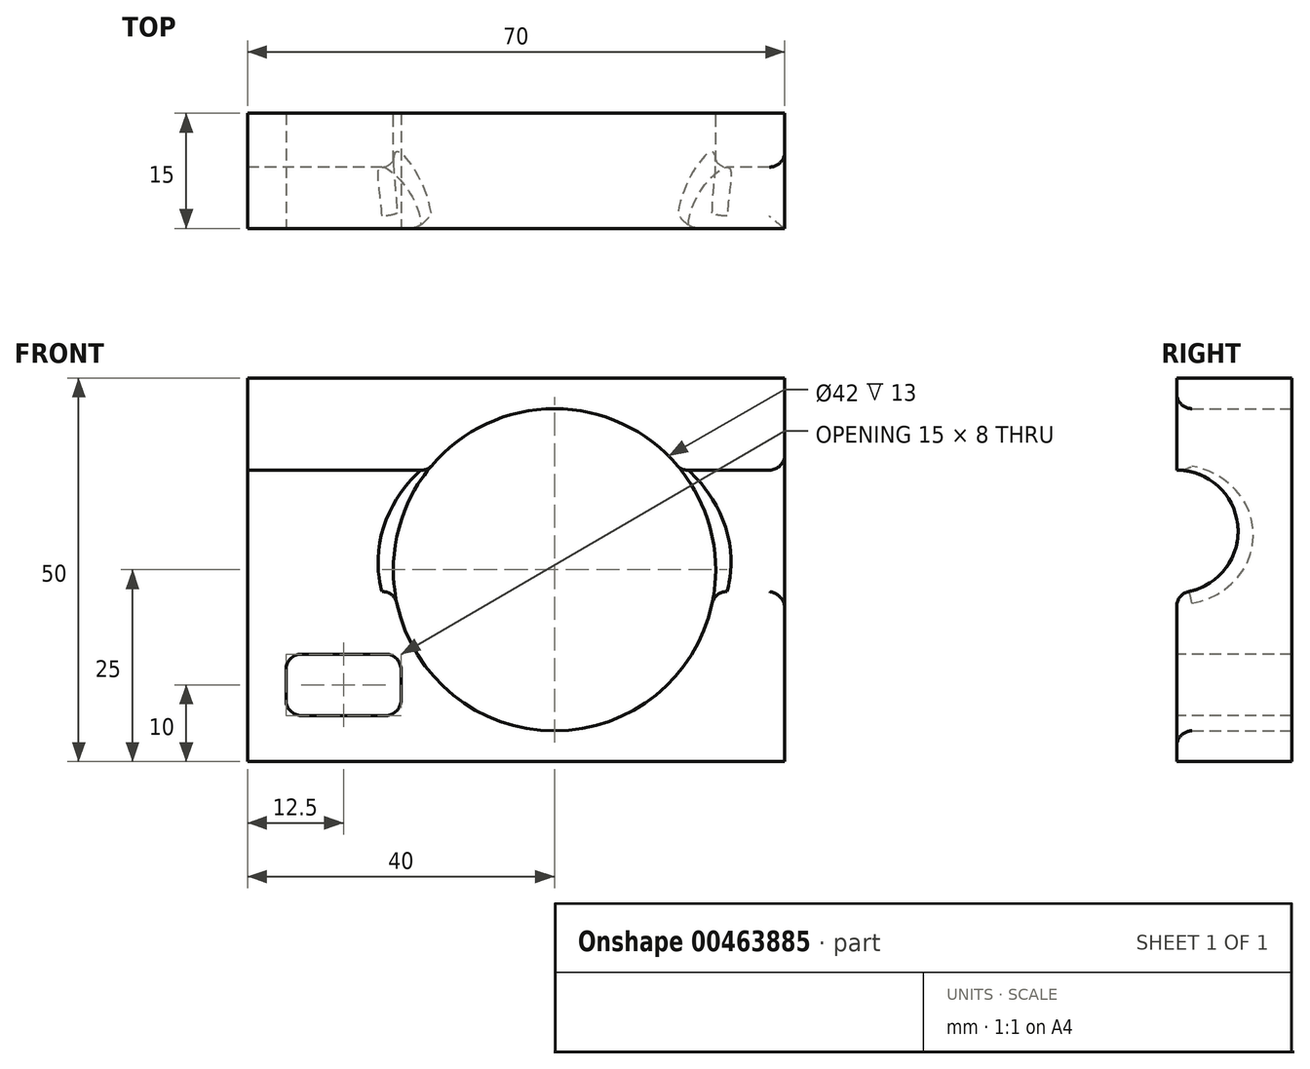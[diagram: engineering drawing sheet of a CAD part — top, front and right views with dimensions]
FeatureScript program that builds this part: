
annotation { "Feature Type Name" : "Feature", "Feature Type Description" : "" }
export const myFeature = defineFeature(function(context is Context, id is Id, definition is map)
    precondition{}
    {
        {
            var Q0;
            Q0=qCreatedBy(makeId("Front.planeOp"),FACE);
            var sketch = newSketch(context, id + "F0", { "sketchPlane" : qUnion([Q0])});
            skCircle(sketch, "E0", {"center": v(0, 0) * mm, "radius": 21 * mm});
            skLineSegment(sketch, "E1.bottom", {"start": v(-40, 25) * mm, "end": v(30, 25) * mm});
            skLineSegment(sketch, "E1.top", {"start": v(-40, -25) * mm, "end": v(30, -25) * mm});
            skLineSegment(sketch, "E1.left", {"start": v(-40, 25) * mm, "end": v(-40, -25) * mm});
            skLineSegment(sketch, "E1.right", {"start": v(30, 25) * mm, "end": v(30, -25) * mm});
            skSolve(sketch);
        }
        {
            var Q0;
            Q0 = qSketchRegion(id + "F0", true);
            extrude(context, id + "F1", {"entities" : qUnion([Q0]), "depth" : 15 * mm});
        }
        {
            var Q0;
            Q0=makeQuery(id+"F1.opExtrude","CAP_FACE",FACE,{"disambiguationData":[OSD([sQuery(id+"F0.wireOp",EDGE,"E0"),sQuery(id+"F0.wireOp",EDGE,"E1.bottom"),sQuery(id+"F0.wireOp",EDGE,"E1.top"),sQuery(id+"F0.wireOp",EDGE,"E1.left"),sQuery(id+"F0.wireOp",EDGE,"E1.right")])],"isStart":false});
            var sketch = newSketch(context, id + "F2", { "sketchPlane" : qUnion([Q0])});
            skLineSegment(sketch, "E2.bottom", {"start": v(-33, -11) * mm, "end": v(-22, -11) * mm});
            skLineSegment(sketch, "E2.top", {"start": v(-33, -19) * mm, "end": v(-22, -19) * mm});
            skLineSegment(sketch, "E2.left", {"start": v(-35, -13) * mm, "end": v(-35, -17) * mm});
            skLineSegment(sketch, "E2.right", {"start": v(-20, -13) * mm, "end": v(-20, -17) * mm});
            skPoint(sketch, "E3.visualSharp", {"position": v(-35, -11) * mm});
            skArc(sketch, "E3.filletArc", {"start": v(-33, -11) * mm, "mid": v(-34.41, -11.59) * mm, "end": v(-35, -13) * mm});
            skPoint(sketch, "E4.visualSharp", {"position": v(-20, -11) * mm});
            skArc(sketch, "E4.filletArc", {"start": v(-20, -13) * mm, "mid": v(-20.59, -11.59) * mm, "end": v(-22, -11) * mm});
            skPoint(sketch, "E5.visualSharp", {"position": v(-35, -19) * mm});
            skArc(sketch, "E5.filletArc", {"start": v(-35, -17) * mm, "mid": v(-34.41, -18.41) * mm, "end": v(-33, -19) * mm});
            skPoint(sketch, "E6.visualSharp", {"position": v(-20, -19) * mm});
            skArc(sketch, "E6.filletArc", {"start": v(-22, -19) * mm, "mid": v(-20.59, -18.41) * mm, "end": v(-20, -17) * mm});
            skSolve(sketch);
        }
        {
            var Q0;
            Q0 = qSketchRegion(id + "F2", true);
            extrude(context, id + "F3", {"entities" : qUnion([Q0]), "operationType" : NewBodyOperationType.REMOVE, "endBound" : BoundingType.THROUGH_ALL, "oppositeDirection" : true, "depth" : 25 * mm, "offsetDistance" : 25 * mm});
        }
        {
            var Q0;
            Q0=makeQuery(id+"F1.opExtrude","SWEPT_FACE",FACE,{"disambiguationData":[OSD([sQuery(id+"F0.wireOp",EDGE,"E1.left")])]});
            var sketch = newSketch(context, id + "F4", { "sketchPlane" : qUnion([Q0])});
            skLineSegment(sketch, "E7.0", {"start": v(15, 13) * mm, "end": v(15, -3) * mm});
            skArc(sketch, "E8", {"start": v(15, 13) * mm, "mid": v(7, 5) * mm, "end": v(15, -3) * mm});
            skPoint(sketch, "E9.orphan", {"position": v(15, 25) * mm});
            skPoint(sketch, "E10.orphan", {"position": v(15, -25) * mm});
            skSolve(sketch);
        }
        {
            var Q0;
            Q0 = qSketchRegion(id + "F4", true);
            extrude(context, id + "F5", {"entities" : qUnion([Q0]), "operationType" : NewBodyOperationType.REMOVE, "endBound" : BoundingType.THROUGH_ALL, "oppositeDirection" : true, "depth" : 25 * mm, "offsetDistance" : 25 * mm});
        }
        {
            var Q0;
            {var subQ1=sQuery(id+"F0.wireOp",EDGE,"E1.left");var subQ2=sQuery(id+"F4.wireOp",EDGE,"E8");var subQ3=sQuery(id+"F4.wireOp",EDGE,"E7.0");Q0=makeQuery(id+"F5.boolean.opBoolean","COPY",EDGE,{"disambiguationData":[TD([makeQuery(id+"F1.opExtrude","SWEPT_FACE",FACE,{"disambiguationData":[OSD([subQ1])]})])],"derivedFrom":makeQuery(id+"F5.opExtrude","SWEPT_EDGE",EDGE,{"disambiguationData":[OSD([subQ1,subQ3,subQ2]),TDD([makeQuery(id+"F4.imprint","INTERSECT",VERTEX,{"disambiguationData":[OD(0.0)],"derivedFrom":[makeQuery(id+"F1.opExtrude","CAP_EDGE",EDGE,{"disambiguationData":[OSD([subQ1])],"isStart":false}),subQ3,subQ2]})])]})});}
            var Q1;
            Q1=makeQuery(id+"F5.boolean.opBoolean","SPLIT",EDGE,{"disambiguationData":[OD(0.0)],"derivedFrom":makeQuery(id+"F1.opExtrude","CAP_EDGE",EDGE,{"disambiguationData":[OSD([sQuery(id+"F0.wireOp",EDGE,"E0")])],"isStart":false})});
            var Q2;
            Q2=makeQuery(id+"F5.boolean.opBoolean","INTERSECT",EDGE,{"disambiguationData":[OD(0.0)],"derivedFrom":[makeQuery(id+"F1.opExtrude","SWEPT_FACE",FACE,{"disambiguationData":[OSD([sQuery(id+"F0.wireOp",EDGE,"E0")])]}),makeQuery(id+"F5.opExtrude","SWEPT_FACE",FACE,{"disambiguationData":[OSD([sQuery(id+"F4.wireOp",EDGE,"E8")])]})]});
            var Q3;
            Q3=makeQuery(id+"F5.boolean.opBoolean","INTERSECT",EDGE,{"disambiguationData":[OD(1.0)],"derivedFrom":[makeQuery(id+"F1.opExtrude","SWEPT_FACE",FACE,{"disambiguationData":[OSD([sQuery(id+"F0.wireOp",EDGE,"E0")])]}),makeQuery(id+"F5.opExtrude","SWEPT_FACE",FACE,{"disambiguationData":[OSD([sQuery(id+"F4.wireOp",EDGE,"E8")])]})]});
            var Q4;
            Q4=makeQuery(id+"F5.boolean.opBoolean","SPLIT",EDGE,{"disambiguationData":[OD(1.0)],"derivedFrom":makeQuery(id+"F1.opExtrude","CAP_EDGE",EDGE,{"disambiguationData":[OSD([sQuery(id+"F0.wireOp",EDGE,"E0")])],"isStart":false})});
            var Q5;
            {var subQ1=sQuery(id+"F0.wireOp",EDGE,"E1.left");var subQ2=sQuery(id+"F4.wireOp",EDGE,"E8");var subQ3=sQuery(id+"F4.wireOp",EDGE,"E7.0");Q5=makeQuery(id+"F5.boolean.opBoolean","COPY",EDGE,{"disambiguationData":[TD([makeQuery(id+"F1.opExtrude","SWEPT_FACE",FACE,{"disambiguationData":[OSD([subQ1])]})])],"derivedFrom":makeQuery(id+"F5.opExtrude","SWEPT_EDGE",EDGE,{"disambiguationData":[OSD([subQ1,subQ3,subQ2]),TDD([makeQuery(id+"F4.imprint","INTERSECT",VERTEX,{"disambiguationData":[OD(1.0)],"derivedFrom":[makeQuery(id+"F1.opExtrude","CAP_EDGE",EDGE,{"disambiguationData":[OSD([subQ1])],"isStart":false}),subQ3,subQ2]})])]})});}
            var Q6;
            Q6=makeQuery(id+"F5.boolean.opBoolean","INTERSECT",EDGE,{"derivedFrom":[makeQuery(id+"F1.opExtrude","SWEPT_FACE",FACE,{"disambiguationData":[OSD([sQuery(id+"F0.wireOp",EDGE,"E1.right")])]}),makeQuery(id+"F5.opExtrude","SWEPT_FACE",FACE,{"disambiguationData":[OSD([sQuery(id+"F4.wireOp",EDGE,"E8")])]})]});
            var Q7;
            {var subQ1=sQuery(id+"F4.wireOp",EDGE,"E8");var subQ2=sQuery(id+"F0.wireOp",EDGE,"E1.right");var subQ3=sQuery(id+"F0.wireOp",EDGE,"E1.left");var subQ4=sQuery(id+"F4.wireOp",EDGE,"E7.0");Q7=makeQuery(id+"F5.boolean.opBoolean","COPY",EDGE,{"disambiguationData":[TD([makeQuery(id+"F1.opExtrude","SWEPT_FACE",FACE,{"disambiguationData":[OSD([subQ2])]})])],"derivedFrom":makeQuery(id+"F5.opExtrude","SWEPT_EDGE",EDGE,{"disambiguationData":[OSD([subQ3,subQ4,subQ1]),TDD([makeQuery(id+"F4.imprint","INTERSECT",VERTEX,{"disambiguationData":[OD(1.0)],"derivedFrom":[makeQuery(id+"F1.opExtrude","CAP_EDGE",EDGE,{"disambiguationData":[OSD([subQ3])],"isStart":false}),subQ4,subQ1]})])]})});}
            var Q8;
            {var subQ1=sQuery(id+"F4.wireOp",EDGE,"E8");var subQ2=sQuery(id+"F0.wireOp",EDGE,"E1.right");var subQ3=sQuery(id+"F0.wireOp",EDGE,"E1.left");var subQ4=sQuery(id+"F4.wireOp",EDGE,"E7.0");Q8=makeQuery(id+"F5.boolean.opBoolean","COPY",EDGE,{"disambiguationData":[TD([makeQuery(id+"F1.opExtrude","SWEPT_FACE",FACE,{"disambiguationData":[OSD([subQ2])]})])],"derivedFrom":makeQuery(id+"F5.opExtrude","SWEPT_EDGE",EDGE,{"disambiguationData":[OSD([subQ3,subQ4,subQ1]),TDD([makeQuery(id+"F4.imprint","INTERSECT",VERTEX,{"disambiguationData":[OD(0.0)],"derivedFrom":[makeQuery(id+"F1.opExtrude","CAP_EDGE",EDGE,{"disambiguationData":[OSD([subQ3])],"isStart":false}),subQ4,subQ1]})])]})});}
            fillet(context, id + "F6", {"entities" : qUnion([Q0, Q1, Q2, Q3, Q4, Q5, Q6, Q7, Q8]), "tangentPropagation" : true, "radius" : 2 * mm, "defaultsChanged" : false, "vertexSettings" : [], "allowEdgeOverflow" : false});
        }
    });
